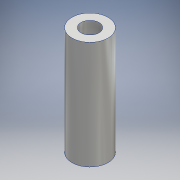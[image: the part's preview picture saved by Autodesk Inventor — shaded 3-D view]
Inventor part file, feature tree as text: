
AUTODESK INVENTOR PART (.ipt)
format: ipt  version: 2020.2 (Build 242310000, 310)  size: 103,424 bytes
history: native  units: mm
features: other x3, extrude x2, sketch x2
ambient origin geometry x8: Origin, YZ Plane, XZ Plane, XY Plane, X Axis, Y Axis, Z Axis, Center Point
bodies: Body1 (feature_tree)
feature tree (7):
  other  "ソリッド1"
  extrude  "押し出し1"  Depth=6.0mm
  other  "作業平面1"
  extrude  "押し出し2"  Depth=3.0mm
  sketch  "スケッチ1"
  sketch  "スケッチ3"
  other  "断面エッジを投影1"
